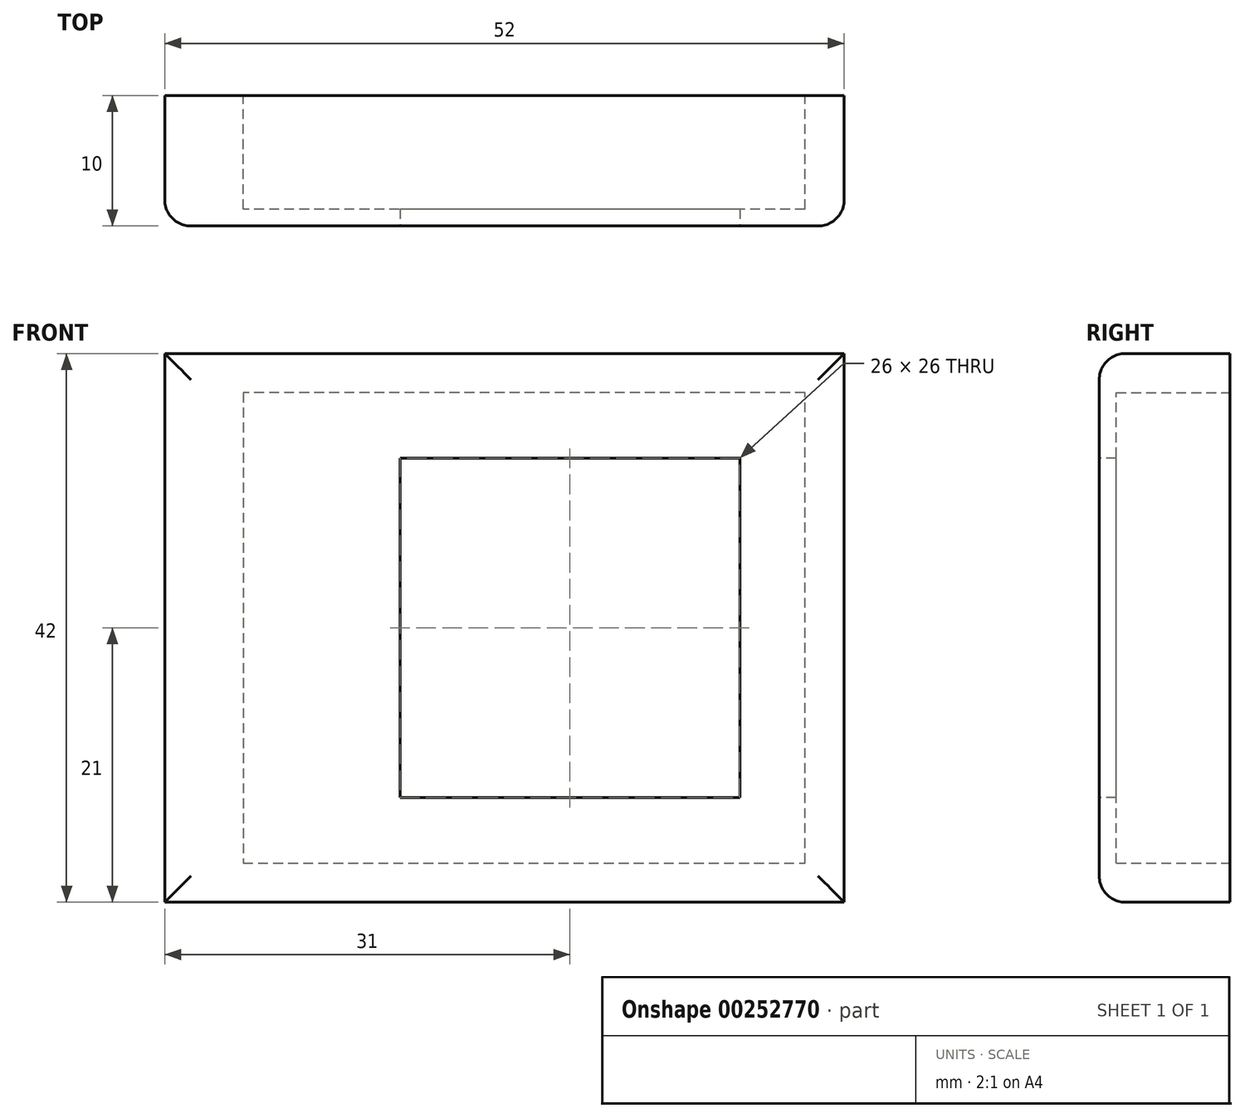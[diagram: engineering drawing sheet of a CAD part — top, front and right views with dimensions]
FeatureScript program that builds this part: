
annotation { "Feature Type Name" : "Feature", "Feature Type Description" : "" }
export const myFeature = defineFeature(function(context is Context, id is Id, definition is map)
    precondition{}
    {
        {
            var Q0;
            Q0=qCreatedBy(makeId("Front.planeOp"),FACE);
            var sketch = newSketch(context, id + "F0", { "sketchPlane" : qUnion([Q0])});
            skLineSegment(sketch, "E0.bottom", {"start": v(26, -21) * mm, "end": v(-26, -21) * mm});
            skLineSegment(sketch, "E0.top", {"start": v(26, 21) * mm, "end": v(-26, 21) * mm});
            skLineSegment(sketch, "E0.left", {"start": v(26, -21) * mm, "end": v(26, 21) * mm});
            skLineSegment(sketch, "E0.right", {"start": v(-26, -21) * mm, "end": v(-26, 21) * mm});
            skPoint(sketch, "E0.middle", {"position": v(0, 0) * mm});
            skSolve(sketch);
        }
        {
            var Q0;
            Q0=makeQuery(id+"F0.imprint","IMPRINT",FACE,{"disambiguationData":[TD([[makeQuery(id+"F0.imprint","IMPRINT",EDGE,{"derivedFrom":sQuery(id+"F0.wireOp",EDGE,"E0.bottom")}),-1.0]])]});
            extrude(context, id + "F1", {"entities" : qUnion([Q0]), "oppositeDirection" : true, "depth" : 10 * mm});
        }
        {
            var Q0;
            Q0=makeQuery(id+"F1.opExtrude","CAP_FACE",FACE,{"disambiguationData":[OSD([sQuery(id+"F0.wireOp",EDGE,"E0.bottom"),sQuery(id+"F0.wireOp",EDGE,"E0.top"),sQuery(id+"F0.wireOp",EDGE,"E0.left"),sQuery(id+"F0.wireOp",EDGE,"E0.right")])],"isStart":true});
            var sketch = newSketch(context, id + "F2", { "sketchPlane" : qUnion([Q0])});
            skLineSegment(sketch, "E1", {"start": v(18, 13) * mm, "end": v(-8, 13) * mm});
            skLineSegment(sketch, "E2", {"start": v(-8, 13) * mm, "end": v(-8, -13) * mm});
            skLineSegment(sketch, "E3", {"start": v(-8, -13) * mm, "end": v(18, -13) * mm});
            skLineSegment(sketch, "E4", {"start": v(18, -13) * mm, "end": v(18, 13) * mm});
            skSolve(sketch);
        }
        {
            var Q0;
            Q0=makeQuery(id+"F2.imprint","IMPRINT",FACE,{"disambiguationData":[TD([[makeQuery(id+"F2.imprint","IMPRINT",EDGE,{"derivedFrom":sQuery(id+"F2.wireOp",EDGE,"E1")}),1.0]])]});
            extrude(context, id + "F3", {"entities" : qUnion([Q0]), "operationType" : NewBodyOperationType.REMOVE, "oppositeDirection" : true, "depth" : 25 * mm});
        }
        {
            var Q0;
            Q0=makeQuery(id+"F1.opExtrude","CAP_FACE",FACE,{"disambiguationData":[OSD([sQuery(id+"F0.wireOp",EDGE,"E0.bottom"),sQuery(id+"F0.wireOp",EDGE,"E0.top"),sQuery(id+"F0.wireOp",EDGE,"E0.left"),sQuery(id+"F0.wireOp",EDGE,"E0.right")])],"isStart":false});
            var sketch = newSketch(context, id + "F4", { "sketchPlane" : qUnion([Q0])});
            skLineSegment(sketch, "E5", {"start": v(-23, 18) * mm, "end": v(20, 18) * mm});
            skLineSegment(sketch, "E6", {"start": v(20, 18) * mm, "end": v(20, -18) * mm});
            skLineSegment(sketch, "E7", {"start": v(20, -18) * mm, "end": v(-23, -18) * mm});
            skLineSegment(sketch, "E8", {"start": v(-23, -18) * mm, "end": v(-23, 18) * mm});
            skSolve(sketch);
        }
        {
            var Q0;
            Q0=makeQuery(id+"F4.imprint","IMPRINT",FACE,{"disambiguationData":[TD([[makeQuery(id+"F4.imprint","IMPRINT",EDGE,{"derivedFrom":sQuery(id+"F4.wireOp",EDGE,"E5")}),-1.0]])]});
            extrude(context, id + "F5", {"entities" : qUnion([Q0]), "operationType" : NewBodyOperationType.REMOVE, "oppositeDirection" : true, "depth" : 8.7 * mm});
        }
        {
            var Q0;
            Q0=makeQuery(id+"F1.opExtrude","CAP_EDGE",EDGE,{"disambiguationData":[OSD([sQuery(id+"F0.wireOp",EDGE,"E0.right")])],"isStart":true});
            var Q1;
            Q1=makeQuery(id+"F1.opExtrude","CAP_EDGE",EDGE,{"disambiguationData":[OSD([sQuery(id+"F0.wireOp",EDGE,"E0.top")])],"isStart":true});
            var Q2;
            Q2=makeQuery(id+"F1.opExtrude","CAP_EDGE",EDGE,{"disambiguationData":[OSD([sQuery(id+"F0.wireOp",EDGE,"E0.left")])],"isStart":true});
            var Q3;
            Q3=makeQuery(id+"F1.opExtrude","CAP_EDGE",EDGE,{"disambiguationData":[OSD([sQuery(id+"F0.wireOp",EDGE,"E0.bottom")])],"isStart":true});
            var Q4;
            Q4=makeQuery(id+"F3.boolean.opBoolean","COPY",EDGE,{"derivedFrom":makeQuery(id+"F3.opExtrude","CAP_EDGE",EDGE,{"disambiguationData":[OSD([sQuery(id+"F2.wireOp",EDGE,"E2")])],"isStart":true})});
            var Q5;
            Q5=makeQuery(id+"F3.boolean.opBoolean","COPY",EDGE,{"derivedFrom":makeQuery(id+"F3.opExtrude","CAP_EDGE",EDGE,{"disambiguationData":[OSD([sQuery(id+"F2.wireOp",EDGE,"E3")])],"isStart":true})});
            var Q6;
            Q6=makeQuery(id+"F3.boolean.opBoolean","COPY",EDGE,{"derivedFrom":makeQuery(id+"F3.opExtrude","CAP_EDGE",EDGE,{"disambiguationData":[OSD([sQuery(id+"F2.wireOp",EDGE,"E4")])],"isStart":true})});
            var Q7;
            Q7=makeQuery(id+"F3.boolean.opBoolean","COPY",EDGE,{"derivedFrom":makeQuery(id+"F3.opExtrude","CAP_EDGE",EDGE,{"disambiguationData":[OSD([sQuery(id+"F2.wireOp",EDGE,"E1")])],"isStart":true})});
            fillet(context, id + "F6", {"entities" : qUnion([Q0, Q1, Q2, Q3, Q4, Q5, Q6, Q7]), "radius" : 2 * mm, "tangentPropagation" : true, "allowEdgeOverflow" : false});
        }
    });
